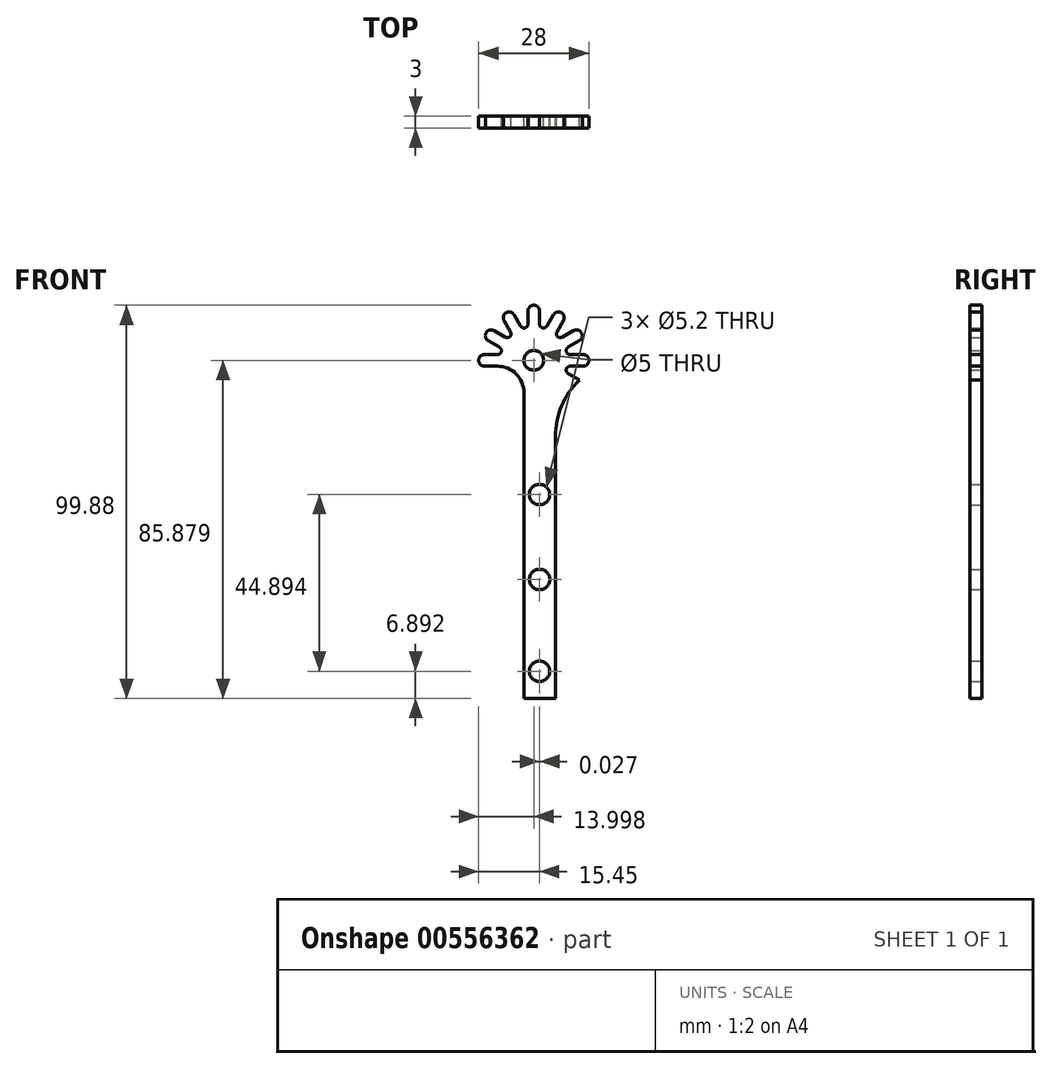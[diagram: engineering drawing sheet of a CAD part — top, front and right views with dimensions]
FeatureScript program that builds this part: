
annotation { "Feature Type Name" : "Feature", "Feature Type Description" : "" }
export const myFeature = defineFeature(function(context is Context, id is Id, definition is map)
    precondition{}
    {
        {
            var Q0;
            Q0=qCreatedBy(makeId("Front.planeOp"),FACE);
            var sketch = newSketch(context, id + "F0", { "sketchPlane" : qUnion([Q0])});
            skCircle(sketch, "E0", {"center": v(-2.37, 26.77) * mm, "radius": 2.5 * mm});
            skArc(sketch, "E1", {"start": v(4.44, 14.54) * mm, "mid": v(4.72, 38.84) * mm, "end": v(-16.37, 26.77) * mm, "construction": true});
            skLineSegment(sketch, "E2.bottom", {"start": v(-4.87, 26.77) * mm, "end": v(0.13, 26.77) * mm, "construction": true});
            skLineSegment(sketch, "E2.left", {"start": v(-4.87, 26.77) * mm, "end": v(-4.87, 26.47) * mm, "construction": true});
            skLineSegment(sketch, "E3", {"start": v(11.63, 26.77) * mm, "end": v(10.16, 26.77) * mm, "construction": true});
            skLineSegment(sketch, "E4", {"start": v(-11.6, 28.24) * mm, "end": v(-14.9, 28.24) * mm});
            skArc(sketch, "E5", {"start": v(-14.9, 28.24) * mm, "mid": v(-16.37, 26.77) * mm, "end": v(-14.9, 25.3) * mm});
            skLineSegment(sketch, "E6", {"start": v(-14.9, 25.3) * mm, "end": v(-11.6, 25.3) * mm});
            skArc(sketch, "E7.1.0", {"start": v(-12.48, 34.3) * mm, "mid": v(-14.5, 33.77) * mm, "end": v(-13.96, 31.75) * mm});
            skLineSegment(sketch, "E7.1.1", {"start": v(-9.63, 32.66) * mm, "end": v(-12.48, 34.3) * mm});
            skLineSegment(sketch, "E7.1.2", {"start": v(-13.96, 31.75) * mm, "end": v(-11.1, 30.1) * mm});
            skArc(sketch, "E7.2.0", {"start": v(-7.36, 38.35) * mm, "mid": v(-9.37, 38.9) * mm, "end": v(-9.91, 36.88) * mm});
            skLineSegment(sketch, "E7.2.1", {"start": v(-5.71, 35.5) * mm, "end": v(-7.36, 38.35) * mm});
            skLineSegment(sketch, "E7.2.2", {"start": v(-9.91, 36.88) * mm, "end": v(-8.27, 34.03) * mm});
            skArc(sketch, "E7.3.0", {"start": v(-0.9, 39.3) * mm, "mid": v(-2.37, 40.77) * mm, "end": v(-3.85, 39.3) * mm});
            skLineSegment(sketch, "E7.3.1", {"start": v(-0.9, 36) * mm, "end": v(-0.9, 39.3) * mm});
            skLineSegment(sketch, "E7.3.2", {"start": v(-3.85, 39.3) * mm, "end": v(-3.85, 36) * mm});
            skArc(sketch, "E7.4.0", {"start": v(5.17, 36.88) * mm, "mid": v(4.63, 38.9) * mm, "end": v(2.62, 38.35) * mm});
            skLineSegment(sketch, "E7.4.1", {"start": v(3.53, 34.03) * mm, "end": v(5.17, 36.88) * mm});
            skLineSegment(sketch, "E7.4.2", {"start": v(2.62, 38.35) * mm, "end": v(0.97, 35.5) * mm});
            skArc(sketch, "E7.5.0", {"start": v(9.22, 31.75) * mm, "mid": v(9.76, 33.77) * mm, "end": v(7.74, 34.3) * mm});
            skLineSegment(sketch, "E7.5.1", {"start": v(6.37, 30.1) * mm, "end": v(9.22, 31.75) * mm});
            skLineSegment(sketch, "E7.5.2", {"start": v(7.74, 34.3) * mm, "end": v(4.9, 32.66) * mm});
            skArc(sketch, "E7.6.0", {"start": v(10.16, 25.3) * mm, "mid": v(11.63, 26.77) * mm, "end": v(10.16, 28.24) * mm});
            skLineSegment(sketch, "E7.6.1", {"start": v(6.87, 25.3) * mm, "end": v(10.16, 25.3) * mm});
            skLineSegment(sketch, "E7.6.2", {"start": v(10.16, 28.24) * mm, "end": v(6.87, 28.24) * mm});
            skLineSegment(sketch, "E7.anchor1", {"start": v(-2.37, 26.77) * mm, "end": v(-4.87, 26.47) * mm, "construction": true});
            skLineSegment(sketch, "E7.anchor2", {"start": v(-2.37, 26.77) * mm, "end": v(0.11, 27.06) * mm, "construction": true});
            skArc(sketch, "E8", {"start": v(-11.6, 28.24) * mm, "mid": v(-10.64, 28.98) * mm, "end": v(-11.1, 30.1) * mm});
            skArc(sketch, "E9.1.0", {"start": v(-9.63, 32.66) * mm, "mid": v(-8.43, 32.82) * mm, "end": v(-8.27, 34.03) * mm});
            skArc(sketch, "E9.2.0", {"start": v(-5.71, 35.5) * mm, "mid": v(-4.59, 35.04) * mm, "end": v(-3.85, 36) * mm});
            skArc(sketch, "E9.3.0", {"start": v(-0.9, 36) * mm, "mid": v(-0.15, 35.04) * mm, "end": v(0.97, 35.5) * mm});
            skArc(sketch, "E9.4.0", {"start": v(3.53, 34.03) * mm, "mid": v(3.68, 32.82) * mm, "end": v(4.9, 32.66) * mm});
            skArc(sketch, "E9.5.0", {"start": v(6.37, 30.1) * mm, "mid": v(5.9, 28.98) * mm, "end": v(6.87, 28.24) * mm});
            skArc(sketch, "E9.6.0", {"start": v(6.87, 25.3) * mm, "mid": v(5.9, 24.55) * mm, "end": v(6.37, 23.43) * mm});
            skLineSegment(sketch, "E9.anchor1", {"start": v(-2.37, 26.77) * mm, "end": v(-4.84, 27.16) * mm, "construction": true});
            skLineSegment(sketch, "E9.anchor2", {"start": v(-2.37, 26.77) * mm, "end": v(0.1, 26.37) * mm, "construction": true});
            skLineSegment(sketch, "E10", {"start": v(6.37, 23.43) * mm, "end": v(9.22, 21.78) * mm});
            skArc(sketch, "E11", {"start": v(-4.87, 18.56) * mm, "mid": v(-6.85, 23.32) * mm, "end": v(-11.6, 25.3) * mm});
            skLineSegment(sketch, "E12", {"start": v(-4.87, 18.56) * mm, "end": v(-4.87, -27.23) * mm});
            skLineSegment(sketch, "E13", {"start": v(3.13, -27.23) * mm, "end": v(3.13, 7.42) * mm});
            skArc(sketch, "E14", {"start": v(9.22, 21.78) * mm, "mid": v(4.72, 15.22) * mm, "end": v(3.13, 7.42) * mm});
            skLineSegment(sketch, "E15.trimOffspring", {"start": v(3.13, 7.42) * mm, "end": v(3.13, -27.23) * mm, "construction": true});
            skLineSegment(sketch, "E16.trimOffspring", {"start": v(-4.87, 18.56) * mm, "end": v(-4.87, -27.23) * mm, "construction": true});
            skLineSegment(sketch, "E17.trimOffspring", {"start": v(3.13, 25.9) * mm, "end": v(6.87, 25.3) * mm, "construction": true});
            skLineSegment(sketch, "E18.trimOffspring", {"start": v(0.13, 26.77) * mm, "end": v(-4.87, 26.77) * mm, "construction": true});
            skLineSegment(sketch, "E19", {"start": v(-4.87, -27.23) * mm, "end": v(-4.87, -59.1) * mm});
            skLineSegment(sketch, "E20", {"start": v(-4.87, -59.1) * mm, "end": v(3.13, -59.1) * mm});
            skLineSegment(sketch, "E21", {"start": v(3.13, -59.1) * mm, "end": v(3.13, -27.23) * mm});
            skCircle(sketch, "E22", {"center": v(-0.92, -7.32) * mm, "radius": 2.6 * mm});
            skCircle(sketch, "E23", {"center": v(-0.9, -28.9) * mm, "radius": 2.6 * mm});
            skCircle(sketch, "E24", {"center": v(-0.92, -52.22) * mm, "radius": 2.6 * mm});
            skSolve(sketch);
        }
        {
            var Q0;
            Q0=makeQuery(id+"F0.imprint","IMPRINT",FACE,{"disambiguationData":[TD([[makeQuery(id+"F0.imprint","IMPRINT",EDGE,{"derivedFrom":sQuery(id+"F0.wireOp",EDGE,"E0")}),-1.0]])]});
            extrude(context, id + "F1", {"entities" : qUnion([Q0]), "depth" : 3 * mm, "offsetDistance" : 25.4 * mm});
        }
    });
